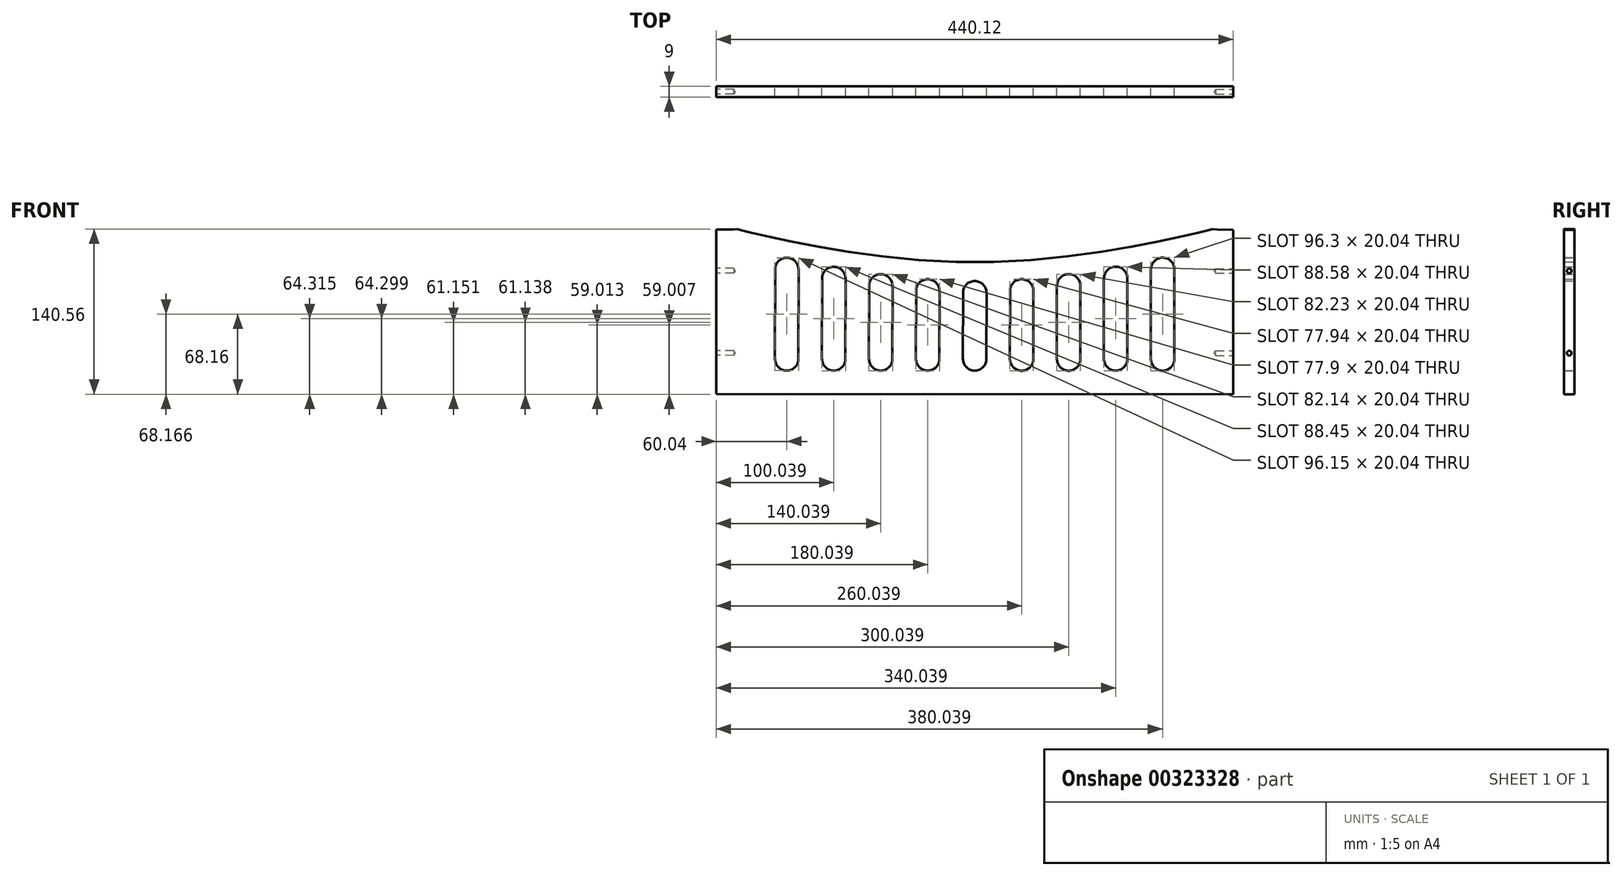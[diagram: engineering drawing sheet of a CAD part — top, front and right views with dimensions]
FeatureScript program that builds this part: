
annotation { "Feature Type Name" : "Feature", "Feature Type Description" : "" }
export const myFeature = defineFeature(function(context is Context, id is Id, definition is map)
    precondition{}
    {
        {
            var Q0;
            Q0=qCreatedBy(makeId("Front.planeOp"),FACE);
            var sketch = newSketch(context, id + "F0", { "sketchPlane" : qUnion([Q0])});
            skLineSegment(sketch, "E0.bottom", {"start": v(219.94, -70.05) * mm, "end": v(-220.06, -69.95) * mm});
            skLineSegment(sketch, "E0.left", {"start": v(219.94, -70.05) * mm, "end": v(220.06, 69.95) * mm});
            skLineSegment(sketch, "E0.right", {"start": v(-220.06, -69.95) * mm, "end": v(-219.94, 70.05) * mm});
            skPoint(sketch, "E0.middle", {"position": v(0, 0) * mm});
            skFitSpline(sketch, "E1", {"points": [v(-219.94, 70.05) * mm, v(-199.94, 70.05) * mm, v(0, 42.34) * mm, v(200.06, 70.05) * mm, v(220.06, 69.95) * mm], "startDerivative": vector(501.28, 0) * mm, "endDerivative": vector(501.28, -2.26) * mm});
            skLineSegment(sketch, "E2", {"start": v(0, 16.34) * mm, "end": v(-0.04, -40) * mm});
            skLineSegment(sketch, "E3.4.0.1", {"start": v(-170, 16.34) * mm, "end": v(-170, 16.34) * mm});
            skLineSegment(sketch, "E4", {"start": v(-120, 28.47) * mm, "end": v(-120.04, -39.98) * mm});
            skLineSegment(sketch, "E5", {"start": v(-80, 22.16) * mm, "end": v(-80.04, -39.98) * mm});
            skLineSegment(sketch, "E6", {"start": v(-40, 17.9) * mm, "end": v(-40.04, -40) * mm});
            skLineSegment(sketch, "E7", {"start": v(40, 17.93) * mm, "end": v(39.96, -40) * mm});
            skLineSegment(sketch, "E8", {"start": v(80, 22.22) * mm, "end": v(79.96, -40.02) * mm});
            skLineSegment(sketch, "E9", {"start": v(120, 28.55) * mm, "end": v(119.96, -40.02) * mm});
            skLineSegment(sketch, "E10", {"start": v(160, 36.27) * mm, "end": v(159.96, -40.03) * mm});
            skArc(sketch, "E11.0.startCap", {"start": v(-170, 36.19) * mm, "mid": v(-160, 46.18) * mm, "end": v(-150, 36.18) * mm});
            skArc(sketch, "E11.0.endCap", {"start": v(-150.05, -39.97) * mm, "mid": v(-160.05, -49.96) * mm, "end": v(-170.04, -39.96) * mm});
            skLineSegment(sketch, "E11.0.left", {"start": v(-150, 36.18) * mm, "end": v(-150.05, -39.97) * mm});
            skLineSegment(sketch, "E11.0.right", {"start": v(-170, 36.19) * mm, "end": v(-170.04, -39.96) * mm});
            skArc(sketch, "E11.1.startCap", {"start": v(-130, 28.48) * mm, "mid": v(-120, 38.47) * mm, "end": v(-110, 28.47) * mm});
            skArc(sketch, "E11.1.endCap", {"start": v(-110.04, -39.98) * mm, "mid": v(-120.05, -49.98) * mm, "end": v(-130.04, -39.97) * mm});
            skLineSegment(sketch, "E11.1.left", {"start": v(-110, 28.47) * mm, "end": v(-110.04, -39.98) * mm});
            skLineSegment(sketch, "E11.1.right", {"start": v(-130, 28.48) * mm, "end": v(-130.04, -39.97) * mm});
            skArc(sketch, "E11.2.startCap", {"start": v(-90, 22.17) * mm, "mid": v(-80, 32.16) * mm, "end": v(-70, 22.15) * mm});
            skArc(sketch, "E11.2.endCap", {"start": v(-70.04, -40) * mm, "mid": v(-80.05, -49.98) * mm, "end": v(-90.04, -39.98) * mm});
            skLineSegment(sketch, "E11.2.left", {"start": v(-70, 22.15) * mm, "end": v(-70.04, -40) * mm});
            skLineSegment(sketch, "E11.2.right", {"start": v(-90, 22.17) * mm, "end": v(-90.04, -39.98) * mm});
            skArc(sketch, "E11.3.startCap", {"start": v(-50, 17.91) * mm, "mid": v(-40, 27.9) * mm, "end": v(-30, 17.9) * mm});
            skArc(sketch, "E11.3.endCap", {"start": v(-30.04, -40) * mm, "mid": v(-40.05, -50) * mm, "end": v(-50.04, -39.98) * mm});
            skLineSegment(sketch, "E11.3.left", {"start": v(-30, 17.9) * mm, "end": v(-30.04, -40) * mm});
            skLineSegment(sketch, "E11.3.right", {"start": v(-50, 17.91) * mm, "end": v(-50.04, -39.98) * mm});
            skArc(sketch, "E11.4.startCap", {"start": v(-10, 16.34) * mm, "mid": v(0, 26.34) * mm, "end": v(10, 16.33) * mm});
            skArc(sketch, "E11.4.endCap", {"start": v(9.96, -40) * mm, "mid": v(-0.05, -50) * mm, "end": v(-10.04, -40) * mm});
            skLineSegment(sketch, "E11.4.left", {"start": v(10, 16.33) * mm, "end": v(9.96, -40) * mm});
            skLineSegment(sketch, "E11.4.right", {"start": v(-10, 16.34) * mm, "end": v(-10.04, -40) * mm});
            skArc(sketch, "E11.5.startCap", {"start": v(30, 17.94) * mm, "mid": v(40, 27.93) * mm, "end": v(50, 17.93) * mm});
            skArc(sketch, "E11.5.endCap", {"start": v(49.96, -40.02) * mm, "mid": v(39.95, -50) * mm, "end": v(29.96, -40) * mm});
            skLineSegment(sketch, "E11.5.left", {"start": v(50, 17.93) * mm, "end": v(49.96, -40.02) * mm});
            skLineSegment(sketch, "E11.5.right", {"start": v(30, 17.94) * mm, "end": v(29.96, -40) * mm});
            skArc(sketch, "E11.6.startCap", {"start": v(70, 22.23) * mm, "mid": v(80, 32.22) * mm, "end": v(90, 22.21) * mm});
            skArc(sketch, "E11.6.endCap", {"start": v(89.96, -40.02) * mm, "mid": v(79.95, -50.02) * mm, "end": v(69.96, -40) * mm});
            skLineSegment(sketch, "E11.6.left", {"start": v(90, 22.21) * mm, "end": v(89.96, -40.02) * mm});
            skLineSegment(sketch, "E11.6.right", {"start": v(70, 22.23) * mm, "end": v(69.96, -40) * mm});
            skArc(sketch, "E11.7.startCap", {"start": v(110, 28.56) * mm, "mid": v(120, 38.55) * mm, "end": v(130, 28.55) * mm});
            skArc(sketch, "E11.7.endCap", {"start": v(129.96, -40.03) * mm, "mid": v(119.95, -50.02) * mm, "end": v(109.96, -40.02) * mm});
            skLineSegment(sketch, "E11.7.left", {"start": v(130, 28.55) * mm, "end": v(129.96, -40.03) * mm});
            skLineSegment(sketch, "E11.7.right", {"start": v(110, 28.56) * mm, "end": v(109.96, -40.02) * mm});
            skArc(sketch, "E11.8.startCap", {"start": v(150, 36.27) * mm, "mid": v(160, 46.27) * mm, "end": v(170, 36.26) * mm});
            skArc(sketch, "E11.8.endCap", {"start": v(169.96, -40.04) * mm, "mid": v(159.95, -50.03) * mm, "end": v(149.96, -40.03) * mm});
            skLineSegment(sketch, "E11.8.left", {"start": v(170, 36.26) * mm, "end": v(169.96, -40.04) * mm});
            skLineSegment(sketch, "E11.8.right", {"start": v(150, 36.27) * mm, "end": v(149.96, -40.03) * mm});
            skSolve(sketch);
        }
        {
            var Q0;
            Q0=makeQuery(id+"F0.imprint","IMPRINT",FACE,{"disambiguationData":[TD([[makeQuery(id+"F0.imprint","IMPRINT",EDGE,{"derivedFrom":sQuery(id+"F0.wireOp",EDGE,"E0.bottom")}),-1.0]])]});
            extrude(context, id + "F1", {"entities" : qUnion([Q0]), "depth" : 9 * mm});
        }
        {
            var Q0;
            Q0=makeQuery(id+"F1.opExtrude","SWEPT_FACE",FACE,{"disambiguationData":[OSD([sQuery(id+"F0.wireOp",EDGE,"E0.right")])]});
            var sketch = newSketch(context, id + "F2", { "sketchPlane" : qUnion([Q0])});
            skLineSegment(sketch, "E12", {"start": v(4.5, 69.85) * mm, "end": v(4.5, -70.15) * mm});
            skPoint(sketch, "E13", {"position": v(4.5, 34.85) * mm});
            skPoint(sketch, "E14", {"position": v(4.5, -35.15) * mm});
            skSolve(sketch);
        }
        {
            var Q0;
            Q0=sQuery(id+"F2.wireOp",VERTEX,"E13");
            var Q1;
            Q1=sQuery(id+"F2.wireOp",VERTEX,"E14");
            var Q2;
            Q2=makeQuery(id+"F1.opExtrude","SWEPT_BODY",BODY,{"disambiguationData":[OSD([sQuery(id+"F0.wireOp",EDGE,"E0.bottom"),sQuery(id+"F0.wireOp",EDGE,"E0.left"),sQuery(id+"F0.wireOp",EDGE,"E0.right"),sQuery(id+"F0.wireOp",EDGE,"E1"),sQuery(id+"F0.wireOp",EDGE,"E11.0.startCap"),sQuery(id+"F0.wireOp",EDGE,"E11.0.endCap"),sQuery(id+"F0.wireOp",EDGE,"E11.0.left"),sQuery(id+"F0.wireOp",EDGE,"E11.0.right"),sQuery(id+"F0.wireOp",EDGE,"E11.1.startCap"),sQuery(id+"F0.wireOp",EDGE,"E11.1.endCap"),sQuery(id+"F0.wireOp",EDGE,"E11.1.left"),sQuery(id+"F0.wireOp",EDGE,"E11.1.right"),sQuery(id+"F0.wireOp",EDGE,"E11.2.startCap"),sQuery(id+"F0.wireOp",EDGE,"E11.2.endCap"),sQuery(id+"F0.wireOp",EDGE,"E11.2.left"),sQuery(id+"F0.wireOp",EDGE,"E11.2.right"),sQuery(id+"F0.wireOp",EDGE,"E11.3.startCap"),sQuery(id+"F0.wireOp",EDGE,"E11.3.endCap"),sQuery(id+"F0.wireOp",EDGE,"E11.3.left"),sQuery(id+"F0.wireOp",EDGE,"E11.3.right"),sQuery(id+"F0.wireOp",EDGE,"E11.4.startCap"),sQuery(id+"F0.wireOp",EDGE,"E11.4.endCap"),sQuery(id+"F0.wireOp",EDGE,"E11.4.left"),sQuery(id+"F0.wireOp",EDGE,"E11.4.right"),sQuery(id+"F0.wireOp",EDGE,"E11.5.startCap"),sQuery(id+"F0.wireOp",EDGE,"E11.5.endCap"),sQuery(id+"F0.wireOp",EDGE,"E11.5.left"),sQuery(id+"F0.wireOp",EDGE,"E11.5.right"),sQuery(id+"F0.wireOp",EDGE,"E11.6.startCap"),sQuery(id+"F0.wireOp",EDGE,"E11.6.endCap"),sQuery(id+"F0.wireOp",EDGE,"E11.6.left"),sQuery(id+"F0.wireOp",EDGE,"E11.6.right"),sQuery(id+"F0.wireOp",EDGE,"E11.7.startCap"),sQuery(id+"F0.wireOp",EDGE,"E11.7.endCap"),sQuery(id+"F0.wireOp",EDGE,"E11.7.left"),sQuery(id+"F0.wireOp",EDGE,"E11.7.right"),sQuery(id+"F0.wireOp",EDGE,"E11.8.startCap"),sQuery(id+"F0.wireOp",EDGE,"E11.8.endCap"),sQuery(id+"F0.wireOp",EDGE,"E11.8.left"),sQuery(id+"F0.wireOp",EDGE,"E11.8.right")])]});
            hole(context, id + "F3", {"style" : HoleStyle.SIMPLE, "endStyle" : HoleEndStyle.BLIND, "holeDiameter" : 4 * mm, "holeDepth" : 15 * mm, "tappedDepth" : 12 * mm, "tapClearance" : 3, "locations" : qUnion([Q0, Q1]), "scope" : qUnion([Q2])});
        }
        {
            var Q0;
            Q0=makeQuery(id+"F1.opExtrude","SWEPT_FACE",FACE,{"disambiguationData":[OSD([sQuery(id+"F0.wireOp",EDGE,"E0.left")])]});
            var sketch = newSketch(context, id + "F4", { "sketchPlane" : qUnion([Q0])});
            skLineSegment(sketch, "E15", {"start": v(-4.5, 70.15) * mm, "end": v(-4.5, -69.85) * mm});
            skPoint(sketch, "E16", {"position": v(-4.5, 35.15) * mm});
            skPoint(sketch, "E17", {"position": v(-4.5, -34.85) * mm});
            skSolve(sketch);
        }
        {
            var Q0;
            Q0=sQuery(id+"F4.wireOp",VERTEX,"E16");
            var Q1;
            Q1=sQuery(id+"F4.wireOp",VERTEX,"E17");
            var Q2;
            Q2=makeQuery(id+"F1.opExtrude","SWEPT_BODY",BODY,{"disambiguationData":[OSD([sQuery(id+"F0.wireOp",EDGE,"E0.bottom"),sQuery(id+"F0.wireOp",EDGE,"E0.left"),sQuery(id+"F0.wireOp",EDGE,"E0.right"),sQuery(id+"F0.wireOp",EDGE,"E1"),sQuery(id+"F0.wireOp",EDGE,"E11.0.startCap"),sQuery(id+"F0.wireOp",EDGE,"E11.0.endCap"),sQuery(id+"F0.wireOp",EDGE,"E11.0.left"),sQuery(id+"F0.wireOp",EDGE,"E11.0.right"),sQuery(id+"F0.wireOp",EDGE,"E11.1.startCap"),sQuery(id+"F0.wireOp",EDGE,"E11.1.endCap"),sQuery(id+"F0.wireOp",EDGE,"E11.1.left"),sQuery(id+"F0.wireOp",EDGE,"E11.1.right"),sQuery(id+"F0.wireOp",EDGE,"E11.2.startCap"),sQuery(id+"F0.wireOp",EDGE,"E11.2.endCap"),sQuery(id+"F0.wireOp",EDGE,"E11.2.left"),sQuery(id+"F0.wireOp",EDGE,"E11.2.right"),sQuery(id+"F0.wireOp",EDGE,"E11.3.startCap"),sQuery(id+"F0.wireOp",EDGE,"E11.3.endCap"),sQuery(id+"F0.wireOp",EDGE,"E11.3.left"),sQuery(id+"F0.wireOp",EDGE,"E11.3.right"),sQuery(id+"F0.wireOp",EDGE,"E11.4.startCap"),sQuery(id+"F0.wireOp",EDGE,"E11.4.endCap"),sQuery(id+"F0.wireOp",EDGE,"E11.4.left"),sQuery(id+"F0.wireOp",EDGE,"E11.4.right"),sQuery(id+"F0.wireOp",EDGE,"E11.5.startCap"),sQuery(id+"F0.wireOp",EDGE,"E11.5.endCap"),sQuery(id+"F0.wireOp",EDGE,"E11.5.left"),sQuery(id+"F0.wireOp",EDGE,"E11.5.right"),sQuery(id+"F0.wireOp",EDGE,"E11.6.startCap"),sQuery(id+"F0.wireOp",EDGE,"E11.6.endCap"),sQuery(id+"F0.wireOp",EDGE,"E11.6.left"),sQuery(id+"F0.wireOp",EDGE,"E11.6.right"),sQuery(id+"F0.wireOp",EDGE,"E11.7.startCap"),sQuery(id+"F0.wireOp",EDGE,"E11.7.endCap"),sQuery(id+"F0.wireOp",EDGE,"E11.7.left"),sQuery(id+"F0.wireOp",EDGE,"E11.7.right"),sQuery(id+"F0.wireOp",EDGE,"E11.8.startCap"),sQuery(id+"F0.wireOp",EDGE,"E11.8.endCap"),sQuery(id+"F0.wireOp",EDGE,"E11.8.left"),sQuery(id+"F0.wireOp",EDGE,"E11.8.right")])]});
            hole(context, id + "F5", {"style" : HoleStyle.SIMPLE, "endStyle" : HoleEndStyle.BLIND, "holeDiameter" : 4 * mm, "holeDepth" : 15 * mm, "tappedDepth" : 12 * mm, "tapClearance" : 3, "locations" : qUnion([Q0, Q1]), "scope" : qUnion([Q2])});
        }
    });
